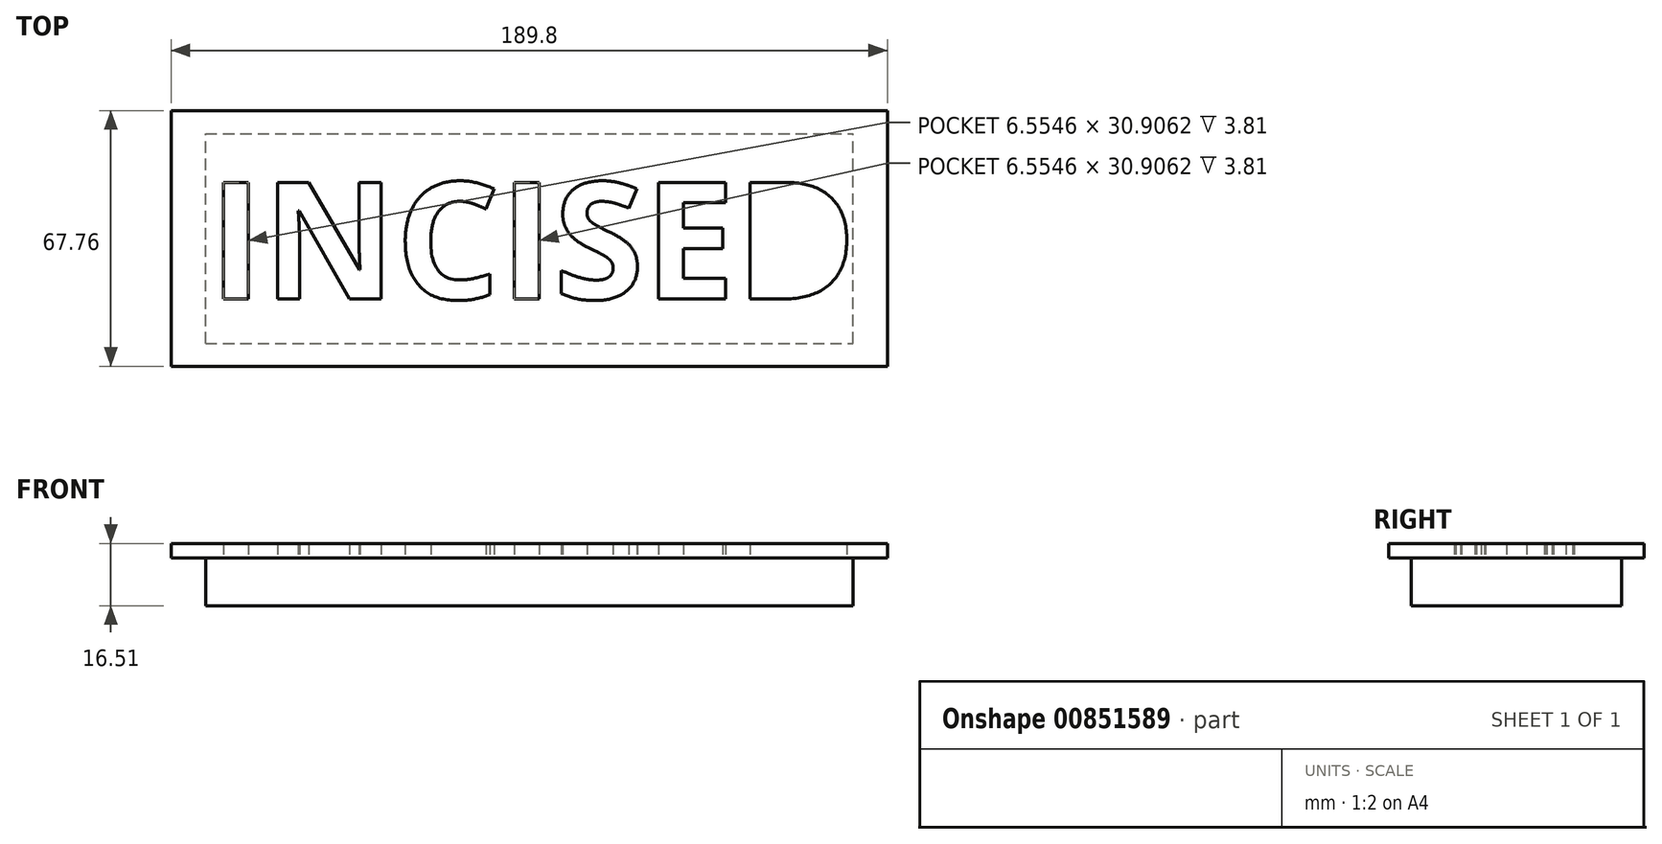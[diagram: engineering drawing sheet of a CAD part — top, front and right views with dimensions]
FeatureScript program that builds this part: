
annotation { "Feature Type Name" : "Feature", "Feature Type Description" : "" }
export const myFeature = defineFeature(function(context is Context, id is Id, definition is map)
    precondition{}
    {
        {
            var Q0;
            Q0=qCreatedBy(makeId("Top.planeOp"),FACE);
            var sketch = newSketch(context, id + "F0", { "sketchPlane" : qUnion([Q0])});
            skLineSegment(sketch, "E0.bottom", {"start": v(94.9, -33.88) * mm, "end": v(-94.9, -33.88) * mm});
            skLineSegment(sketch, "E0.top", {"start": v(94.9, 33.88) * mm, "end": v(-94.9, 33.88) * mm});
            skLineSegment(sketch, "E0.left", {"start": v(94.9, -33.88) * mm, "end": v(94.9, 33.88) * mm});
            skLineSegment(sketch, "E0.right", {"start": v(-94.9, -33.88) * mm, "end": v(-94.9, 33.88) * mm});
            skPoint(sketch, "E0.middle", {"position": v(0, 0) * mm});
            skText(sketch, "E1", { "text": "INCISED", "fontName": "OpenSans-Bold.ttf"});
            const initialGuessF0  = {"E1": [-0.08492, -0.01603, 1, 0, 0.03117]};
            skSetInitialGuess(sketch, initialGuessF0);
            skSolve(sketch);
        }
        {
            var Q0;
            Q0=makeQuery(id+"F0.imprint","IMPRINT",FACE,{"disambiguationData":[TD([[makeQuery(id+"F0.imprint","IMPRINT",EDGE,{"derivedFrom":sQuery(id+"F0.wireOp",EDGE,"E0.bottom")}),-1.0]])]});
            extrude(context, id + "F1", {"entities" : qUnion([Q0]), "depth" : 3.8 * mm, "offsetDistance" : 25.4 * mm});
        }
        {
            var Q0;
            Q0=makeQuery(id+"F1.opExtrude","CAP_FACE",FACE,{"disambiguationData":[OSD([sQuery(id+"F0.wireOp",EDGE,"E0.bottom"),sQuery(id+"F0.wireOp",EDGE,"E0.top"),sQuery(id+"F0.wireOp",EDGE,"E0.left"),sQuery(id+"F0.wireOp",EDGE,"E0.right"),sQuery(id+"F0.wireOp",EDGE,"E1.sketch_text.stroke-0"),sQuery(id+"F0.wireOp",EDGE,"E1.sketch_text.stroke-1"),sQuery(id+"F0.wireOp",EDGE,"E1.sketch_text.stroke-2"),sQuery(id+"F0.wireOp",EDGE,"E1.sketch_text.stroke-3"),sQuery(id+"F0.wireOp",EDGE,"E1.sketch_text.stroke-4"),sQuery(id+"F0.wireOp",EDGE,"E1.sketch_text.stroke-5"),sQuery(id+"F0.wireOp",EDGE,"E1.sketch_text.stroke-6"),sQuery(id+"F0.wireOp",EDGE,"E1.sketch_text.stroke-7"),sQuery(id+"F0.wireOp",EDGE,"E1.sketch_text.stroke-8"),sQuery(id+"F0.wireOp",EDGE,"E1.sketch_text.stroke-9"),sQuery(id+"F0.wireOp",EDGE,"E1.sketch_text.stroke-10"),sQuery(id+"F0.wireOp",EDGE,"E1.sketch_text.stroke-11"),sQuery(id+"F0.wireOp",EDGE,"E1.sketch_text.stroke-12"),sQuery(id+"F0.wireOp",EDGE,"E1.sketch_text.stroke-13"),sQuery(id+"F0.wireOp",EDGE,"E1.sketch_text.stroke-14"),sQuery(id+"F0.wireOp",EDGE,"E1.sketch_text.stroke-15"),sQuery(id+"F0.wireOp",EDGE,"E1.sketch_text.stroke-16"),sQuery(id+"F0.wireOp",EDGE,"E1.sketch_text.stroke-17"),sQuery(id+"F0.wireOp",EDGE,"E1.sketch_text.stroke-18"),sQuery(id+"F0.wireOp",EDGE,"E1.sketch_text.stroke-19"),sQuery(id+"F0.wireOp",EDGE,"E1.sketch_text.stroke-20"),sQuery(id+"F0.wireOp",EDGE,"E1.sketch_text.stroke-21"),sQuery(id+"F0.wireOp",EDGE,"E1.sketch_text.stroke-22"),sQuery(id+"F0.wireOp",EDGE,"E1.sketch_text.stroke-23"),sQuery(id+"F0.wireOp",EDGE,"E1.sketch_text.stroke-24"),sQuery(id+"F0.wireOp",EDGE,"E1.sketch_text.stroke-25"),sQuery(id+"F0.wireOp",EDGE,"E1.sketch_text.stroke-26"),sQuery(id+"F0.wireOp",EDGE,"E1.sketch_text.stroke-27"),sQuery(id+"F0.wireOp",EDGE,"E1.sketch_text.stroke-28"),sQuery(id+"F0.wireOp",EDGE,"E1.sketch_text.stroke-29"),sQuery(id+"F0.wireOp",EDGE,"E1.sketch_text.stroke-30"),sQuery(id+"F0.wireOp",EDGE,"E1.sketch_text.stroke-31"),sQuery(id+"F0.wireOp",EDGE,"E1.sketch_text.stroke-32"),sQuery(id+"F0.wireOp",EDGE,"E1.sketch_text.stroke-33"),sQuery(id+"F0.wireOp",EDGE,"E1.sketch_text.stroke-34"),sQuery(id+"F0.wireOp",EDGE,"E1.sketch_text.stroke-35"),sQuery(id+"F0.wireOp",EDGE,"E1.sketch_text.stroke-36"),sQuery(id+"F0.wireOp",EDGE,"E1.sketch_text.stroke-37"),sQuery(id+"F0.wireOp",EDGE,"E1.sketch_text.stroke-38"),sQuery(id+"F0.wireOp",EDGE,"E1.sketch_text.stroke-39"),sQuery(id+"F0.wireOp",EDGE,"E1.sketch_text.stroke-40"),sQuery(id+"F0.wireOp",EDGE,"E1.sketch_text.stroke-41"),sQuery(id+"F0.wireOp",EDGE,"E1.sketch_text.stroke-42"),sQuery(id+"F0.wireOp",EDGE,"E1.sketch_text.stroke-43"),sQuery(id+"F0.wireOp",EDGE,"E1.sketch_text.stroke-44"),sQuery(id+"F0.wireOp",EDGE,"E1.sketch_text.stroke-45"),sQuery(id+"F0.wireOp",EDGE,"E1.sketch_text.stroke-46"),sQuery(id+"F0.wireOp",EDGE,"E1.sketch_text.stroke-47"),sQuery(id+"F0.wireOp",EDGE,"E1.sketch_text.stroke-48"),sQuery(id+"F0.wireOp",EDGE,"E1.sketch_text.stroke-49"),sQuery(id+"F0.wireOp",EDGE,"E1.sketch_text.stroke-50"),sQuery(id+"F0.wireOp",EDGE,"E1.sketch_text.stroke-51"),sQuery(id+"F0.wireOp",EDGE,"E1.sketch_text.stroke-52"),sQuery(id+"F0.wireOp",EDGE,"E1.sketch_text.stroke-53"),sQuery(id+"F0.wireOp",EDGE,"E1.sketch_text.stroke-54"),sQuery(id+"F0.wireOp",EDGE,"E1.sketch_text.stroke-55"),sQuery(id+"F0.wireOp",EDGE,"E1.sketch_text.stroke-56"),sQuery(id+"F0.wireOp",EDGE,"E1.sketch_text.stroke-57"),sQuery(id+"F0.wireOp",EDGE,"E1.sketch_text.stroke-58"),sQuery(id+"F0.wireOp",EDGE,"E1.sketch_text.stroke-59"),sQuery(id+"F0.wireOp",EDGE,"E1.sketch_text.stroke-60"),sQuery(id+"F0.wireOp",EDGE,"E1.sketch_text.stroke-61"),sQuery(id+"F0.wireOp",EDGE,"E1.sketch_text.stroke-62"),sQuery(id+"F0.wireOp",EDGE,"E1.sketch_text.stroke-63"),sQuery(id+"F0.wireOp",EDGE,"E1.sketch_text.stroke-64"),sQuery(id+"F0.wireOp",EDGE,"E1.sketch_text.stroke-65"),sQuery(id+"F0.wireOp",EDGE,"E1.sketch_text.stroke-66"),sQuery(id+"F0.wireOp",EDGE,"E1.sketch_text.stroke-67"),sQuery(id+"F0.wireOp",EDGE,"E1.sketch_text.stroke-68"),sQuery(id+"F0.wireOp",EDGE,"E1.sketch_text.stroke-69"),sQuery(id+"F0.wireOp",EDGE,"E1.sketch_text.stroke-70"),sQuery(id+"F0.wireOp",EDGE,"E1.sketch_text.stroke-71"),sQuery(id+"F0.wireOp",EDGE,"E1.sketch_text.stroke-72"),sQuery(id+"F0.wireOp",EDGE,"E1.sketch_text.stroke-73"),sQuery(id+"F0.wireOp",EDGE,"E1.sketch_text.stroke-74"),sQuery(id+"F0.wireOp",EDGE,"E1.sketch_text.stroke-75"),sQuery(id+"F0.wireOp",EDGE,"E1.sketch_text.stroke-76"),sQuery(id+"F0.wireOp",EDGE,"E1.sketch_text.stroke-77"),sQuery(id+"F0.wireOp",EDGE,"E1.sketch_text.stroke-78"),sQuery(id+"F0.wireOp",EDGE,"E1.sketch_text.stroke-79"),sQuery(id+"F0.wireOp",EDGE,"E1.sketch_text.stroke-80"),sQuery(id+"F0.wireOp",EDGE,"E1.sketch_text.stroke-81"),sQuery(id+"F0.wireOp",EDGE,"E1.sketch_text.stroke-82"),sQuery(id+"F0.wireOp",EDGE,"E1.sketch_text.stroke-83")])],"isStart":true});
            var sketch = newSketch(context, id + "F2", { "sketchPlane" : qUnion([Q0])});
            skLineSegment(sketch, "E2.bottom", {"start": v(-85.78, 27.84) * mm, "end": v(85.78, 27.84) * mm});
            skLineSegment(sketch, "E2.top", {"start": v(-85.78, -27.84) * mm, "end": v(85.78, -27.84) * mm});
            skLineSegment(sketch, "E2.left", {"start": v(-85.78, 27.84) * mm, "end": v(-85.78, -27.84) * mm});
            skLineSegment(sketch, "E2.right", {"start": v(85.78, 27.84) * mm, "end": v(85.78, -27.84) * mm});
            skPoint(sketch, "E2.middle", {"position": v(0, 0) * mm});
            skSolve(sketch);
        }
        {
            var Q0;
            Q0 = qSketchRegion(id + "F2", true);
            extrude(context, id + "F3", {"entities" : qUnion([Q0]), "operationType" : NewBodyOperationType.REMOVE, "depth" : 5.08 * mm, "offsetDistance" : 25.4 * mm});
        }
        {
            var Q0;
            Q0 = qSketchRegion(id + "F2", true);
            extrude(context, id + "F4", {"entities" : qUnion([Q0]), "operationType" : NewBodyOperationType.ADD, "depth" : 12.7 * mm, "offsetDistance" : 25.4 * mm});
        }
    });
